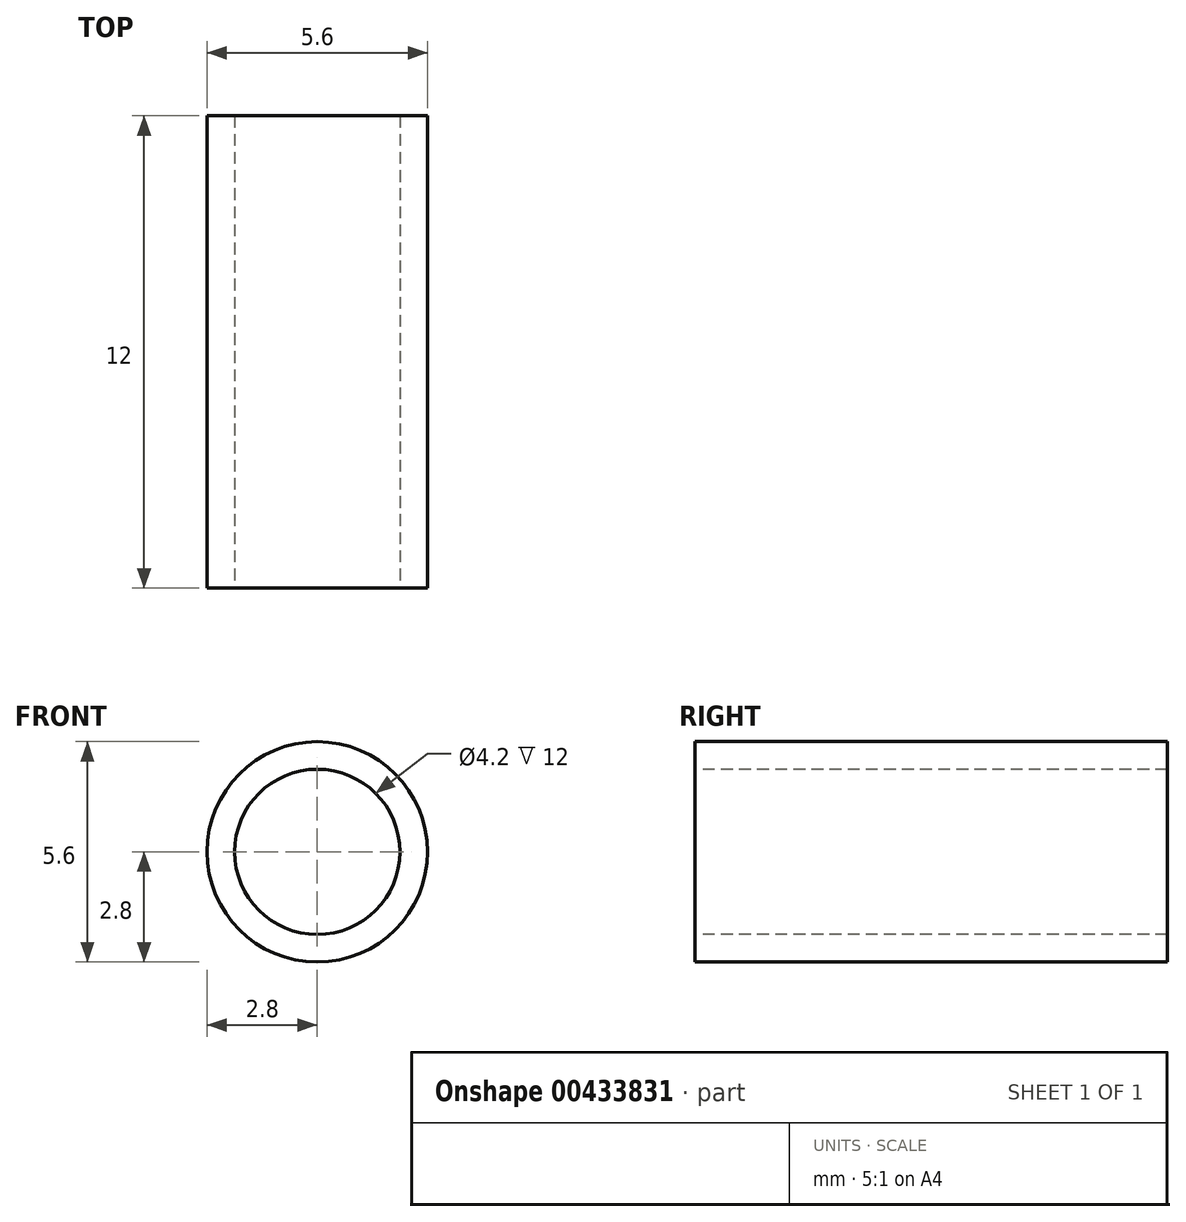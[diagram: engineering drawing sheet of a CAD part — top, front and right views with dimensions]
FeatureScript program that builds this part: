
annotation { "Feature Type Name" : "Feature", "Feature Type Description" : "" }
export const myFeature = defineFeature(function(context is Context, id is Id, definition is map)
    precondition{}
    {
        {
            var Q0;
            Q0=qCreatedBy(makeId("Front.planeOp"),FACE);
            var sketch = newSketch(context, id + "F0", { "sketchPlane" : qUnion([Q0])});
            skCircle(sketch, "E0", {"center": v(0, 0) * mm, "radius": 2.1 * mm});
            skCircle(sketch, "E1", {"center": v(0, 0) * mm, "radius": 2.8 * mm});
            skSolve(sketch);
        }
        {
            var Q0;
            Q0 = qSketchRegion(id + "F0", true);
            extrude(context, id + "F1", {"entities" : qUnion([Q0]), "oppositeDirection" : true, "depth" : 12 * mm});
        }
    });
